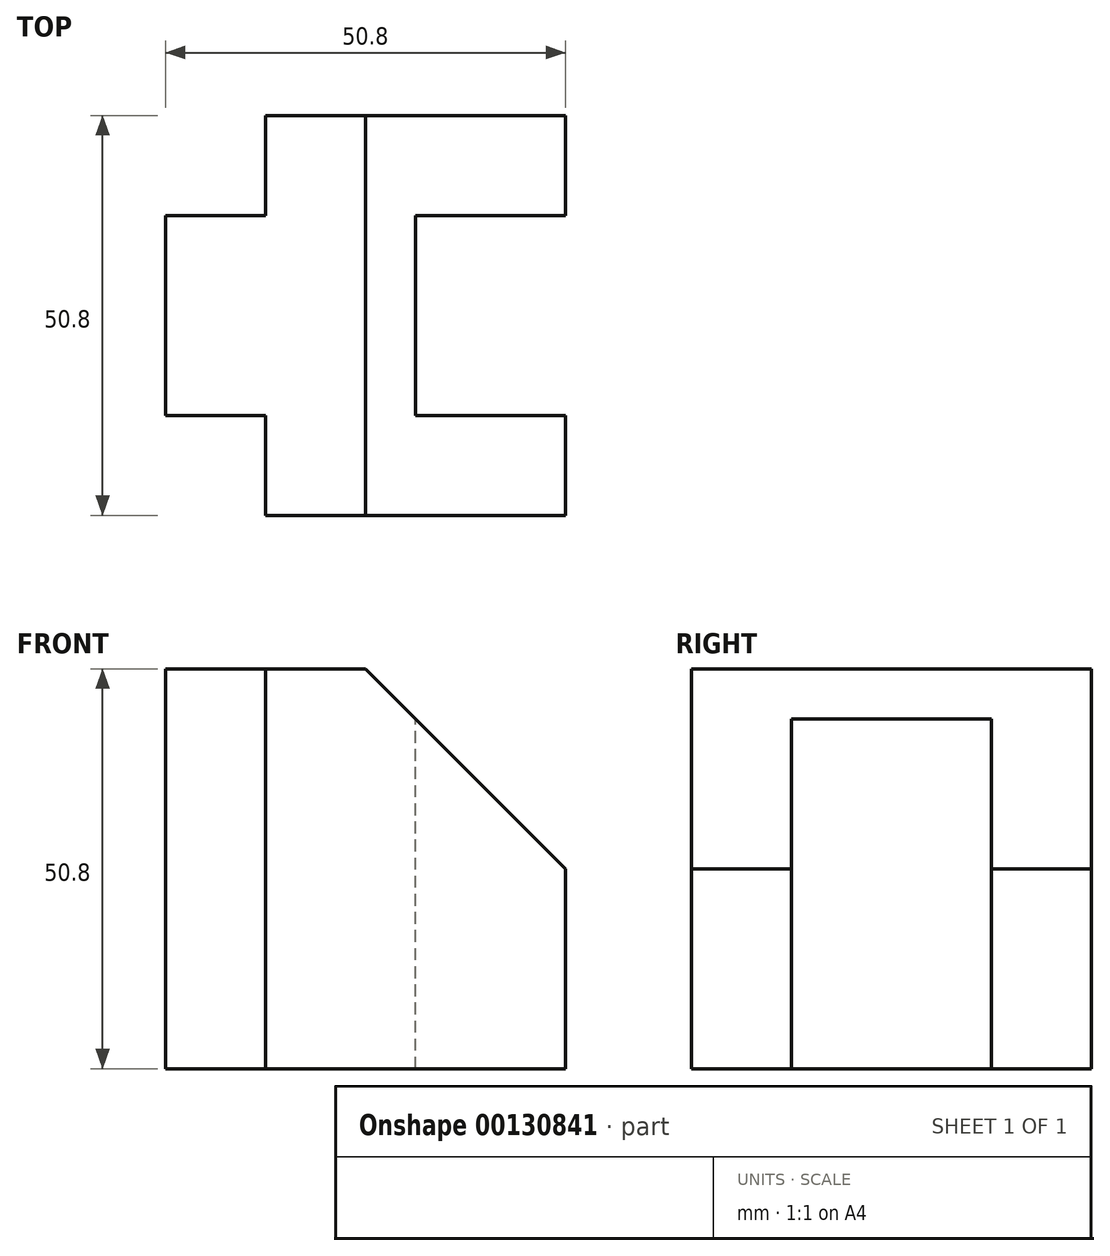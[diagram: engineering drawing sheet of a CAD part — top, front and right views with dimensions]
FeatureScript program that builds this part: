
annotation { "Feature Type Name" : "Feature", "Feature Type Description" : "" }
export const myFeature = defineFeature(function(context is Context, id is Id, definition is map)
    precondition{}
    {
        {
            var Q0;
            Q0=qCreatedBy(makeId("Front.planeOp"),FACE);
            var sketch = newSketch(context, id + "F0", { "sketchPlane" : qUnion([Q0])});
            skLineSegment(sketch, "E0.bottom", {"start": v(0, 0) * mm, "end": v(12.7, 0) * mm});
            skLineSegment(sketch, "E0.top", {"start": v(0, 50.8) * mm, "end": v(12.7, 50.8) * mm});
            skLineSegment(sketch, "E0.left", {"start": v(0, 0) * mm, "end": v(0, 50.8) * mm});
            skLineSegment(sketch, "E0.right", {"start": v(12.7, 0) * mm, "end": v(12.7, 50.8) * mm});
            skLineSegment(sketch, "E1", {"start": v(12.7, 50.8) * mm, "end": v(25.4, 50.8) * mm});
            skLineSegment(sketch, "E2", {"start": v(12.7, 0) * mm, "end": v(50.8, 0) * mm});
            skLineSegment(sketch, "E3", {"start": v(25.4, 50.8) * mm, "end": v(50.8, 25.4) * mm});
            skLineSegment(sketch, "E4", {"start": v(50.8, 25.4) * mm, "end": v(50.8, 0) * mm});
            skSolve(sketch);
        }
        {
            var Q0;
            Q0=makeQuery(id+"F0.imprint","IMPRINT",FACE,{"disambiguationData":[TD([[makeQuery(id+"F0.imprint","IMPRINT",EDGE,{"derivedFrom":sQuery(id+"F0.wireOp",EDGE,"E0.right")}),-1.0]])]});
            var Q1;
            Q1=makeQuery(id+"F0.imprint","IMPRINT",FACE,{"disambiguationData":[TD([[makeQuery(id+"F0.imprint","IMPRINT",EDGE,{"derivedFrom":sQuery(id+"F0.wireOp",EDGE,"E0.bottom")}),1.0]])]});
            extrude(context, id + "F1", {"entities" : qUnion([Q0, Q1]), "endBound" : BoundingType.SYMMETRIC, "depth" : 50.8 * mm});
        }
        {
            var Q0;
            Q0=makeQuery(id+"F1.opExtrude","SWEPT_FACE",FACE,{"disambiguationData":[OSD([sQuery(id+"F0.wireOp",EDGE,"E0.top"),sQuery(id+"F0.wireOp",EDGE,"E1")])]});
            var sketch = newSketch(context, id + "F2", { "sketchPlane" : qUnion([Q0])});
            skLineSegment(sketch, "E5", {"start": v(-18.61, 0) * mm, "end": v(91.98, 0) * mm, "construction": true});
            skLineSegment(sketch, "E6.bottom", {"start": v(0, -12.7) * mm, "end": v(12.7, -12.7) * mm});
            skLineSegment(sketch, "E6.top", {"start": v(0, -25.4) * mm, "end": v(12.7, -25.4) * mm});
            skLineSegment(sketch, "E6.left", {"start": v(0, -12.7) * mm, "end": v(0, -25.4) * mm});
            skLineSegment(sketch, "E6.right", {"start": v(12.7, -12.7) * mm, "end": v(12.7, -25.4) * mm});
            skLineSegment(sketch, "E7.bottom", {"start": v(0, 12.7) * mm, "end": v(12.7, 12.7) * mm});
            skLineSegment(sketch, "E7.top", {"start": v(0, 25.4) * mm, "end": v(12.7, 25.4) * mm});
            skLineSegment(sketch, "E7.left", {"start": v(0, 12.7) * mm, "end": v(0, 25.4) * mm});
            skLineSegment(sketch, "E7.right", {"start": v(12.7, 12.7) * mm, "end": v(12.7, 25.4) * mm});
            skLineSegment(sketch, "E8.0", {"start": v(50.8, -25.4) * mm, "end": v(50.8, 25.4) * mm});
            skLineSegment(sketch, "E9.bottom", {"start": v(50.8, 12.7) * mm, "end": v(31.75, 12.7) * mm});
            skLineSegment(sketch, "E9.top", {"start": v(50.8, -12.7) * mm, "end": v(31.75, -12.7) * mm});
            skLineSegment(sketch, "E9.left", {"start": v(50.8, 12.7) * mm, "end": v(50.8, -12.7) * mm});
            skLineSegment(sketch, "E9.right", {"start": v(31.75, 12.7) * mm, "end": v(31.75, -12.7) * mm});
            skSolve(sketch);
        }
        {
            var Q0;
            Q0=makeQuery(id+"F2.imprint","IMPRINT",FACE,{"disambiguationData":[TD([[makeQuery(id+"F2.imprint","IMPRINT",EDGE,{"derivedFrom":sQuery(id+"F2.wireOp",EDGE,"E7.bottom")}),1.0]])]});
            var Q1;
            Q1=makeQuery(id+"F2.imprint","IMPRINT",FACE,{"disambiguationData":[TD([[makeQuery(id+"F2.imprint","IMPRINT",EDGE,{"derivedFrom":sQuery(id+"F2.wireOp",EDGE,"E6.bottom")}),-1.0]])]});
            var Q2;
            Q2=makeQuery(id+"F2.imprint","IMPRINT",FACE,{"disambiguationData":[TD([[makeQuery(id+"F2.imprint","IMPRINT",EDGE,{"derivedFrom":sQuery(id+"F2.wireOp",EDGE,"E9.bottom")}),1.0]])]});
            extrude(context, id + "F3", {"entities" : qUnion([Q0, Q1, Q2]), "operationType" : NewBodyOperationType.REMOVE, "endBound" : BoundingType.THROUGH_ALL, "oppositeDirection" : true, "depth" : 25.4 * mm});
        }
    });
